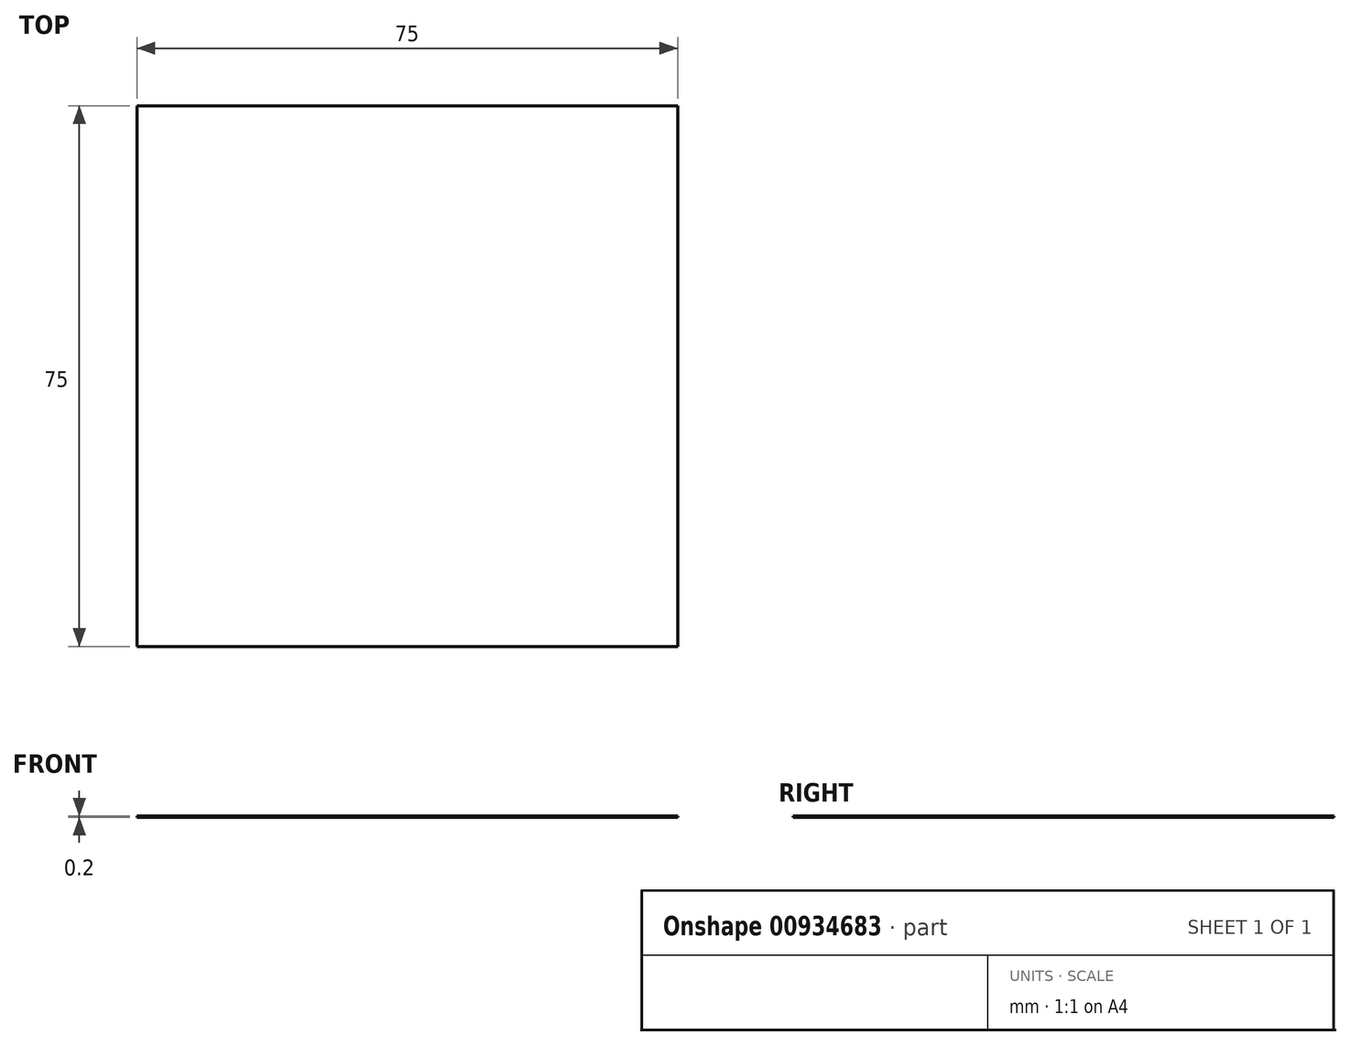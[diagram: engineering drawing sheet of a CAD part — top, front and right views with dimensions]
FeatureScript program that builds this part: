
annotation { "Feature Type Name" : "Feature", "Feature Type Description" : "" }
export const myFeature = defineFeature(function(context is Context, id is Id, definition is map)
    precondition{}
    {
        {
            var Q0;
            Q0=qCreatedBy(makeId("Top.planeOp"),FACE);
            var sketch = newSketch(context, id + "F0", { "sketchPlane" : qUnion([Q0])});
            skLineSegment(sketch, "E0.bottom", {"start": v(37.5, -37.5) * mm, "end": v(-37.5, -37.5) * mm});
            skLineSegment(sketch, "E0.top", {"start": v(37.5, 37.5) * mm, "end": v(-37.5, 37.5) * mm});
            skLineSegment(sketch, "E0.left", {"start": v(37.5, -37.5) * mm, "end": v(37.5, 37.5) * mm});
            skLineSegment(sketch, "E0.right", {"start": v(-37.5, -37.5) * mm, "end": v(-37.5, 37.5) * mm});
            skPoint(sketch, "E0.middle", {"position": v(0, 0) * mm});
            skSolve(sketch);
        }
        {
            var Q0;
            Q0=makeQuery(id+"F0.imprint","IMPRINT",FACE,{"disambiguationData":[TD([[makeQuery(id+"F0.imprint","IMPRINT",EDGE,{"derivedFrom":sQuery(id+"F0.wireOp",EDGE,"E0.bottom")}),-1.0]])]});
            extrude(context, id + "F1", {"entities" : qUnion([Q0]), "depth" : 0.2 * mm, "offsetDistance" : 25 * mm});
        }
    });
